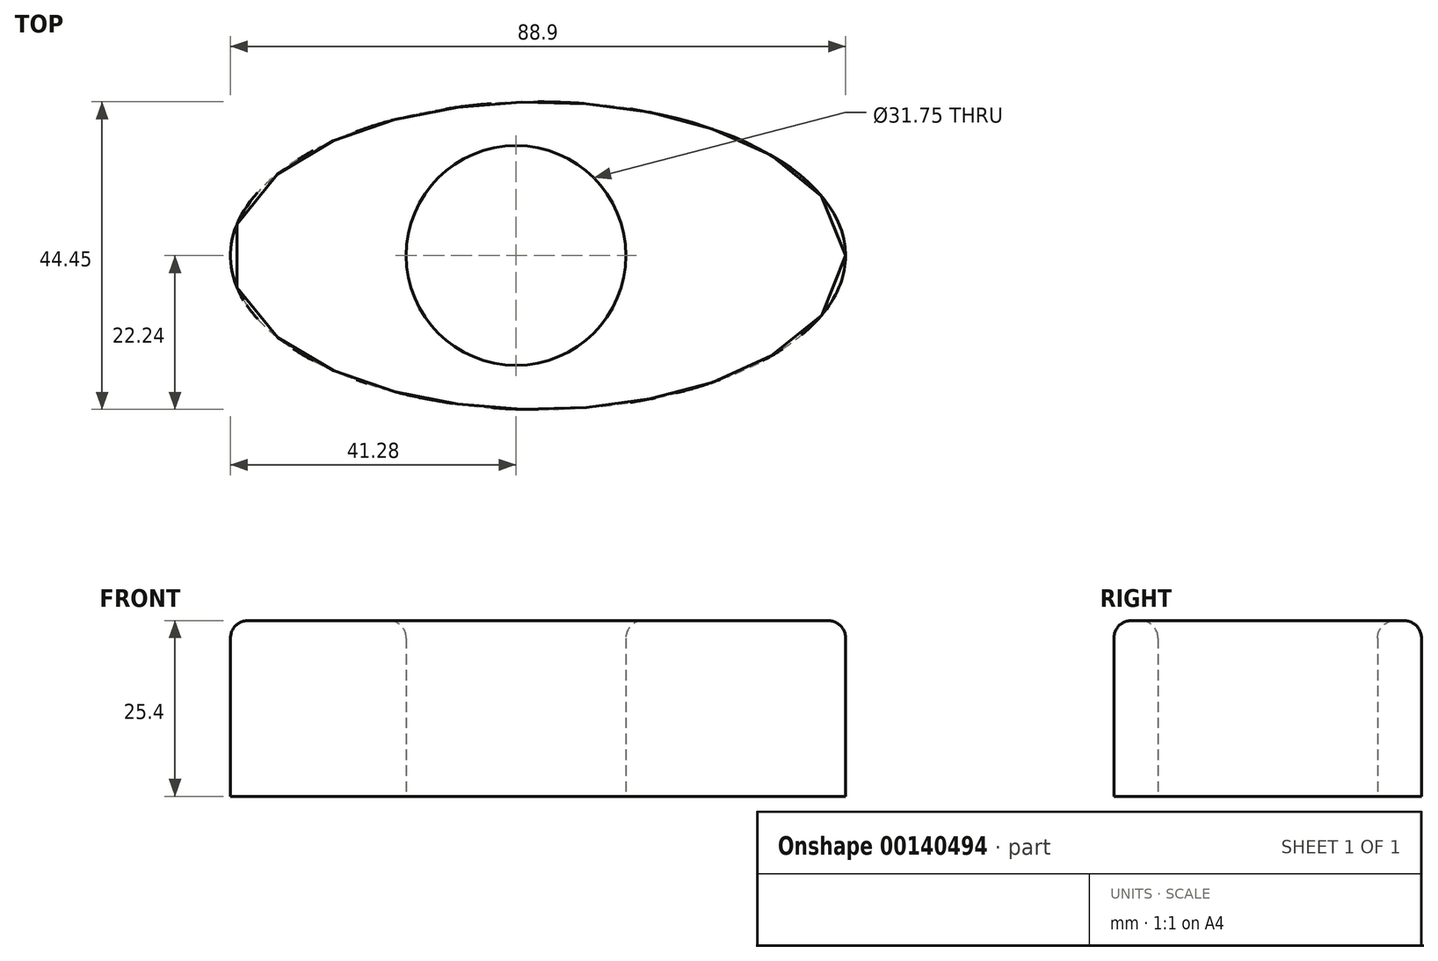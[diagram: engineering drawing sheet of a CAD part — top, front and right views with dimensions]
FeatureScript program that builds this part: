
annotation { "Feature Type Name" : "Feature", "Feature Type Description" : "" }
export const myFeature = defineFeature(function(context is Context, id is Id, definition is map)
    precondition{}
    {
        {
            var Q0;
            Q0=qCreatedBy(makeId("Top.planeOp"),FACE);
            var sketch = newSketch(context, id + "F0", { "sketchPlane" : qUnion([Q0])});
            skCircle(sketch, "E0", {"center": v(0, 0) * mm, "radius": 15.88 * mm});
            skEllipse(sketch, "E1", {"center": v(3.17, -0.02) * mm, "majorRadius": 44.45 * mm, "minorRadius": 22.23 * mm, "majorAxis": v(1, 0)});
            skLineSegment(sketch, "E2.direction1", {"start": v(0, 0) * mm, "end": v(47.62, 0) * mm, "construction": true});
            skLineSegment(sketch, "E3", {"start": v(-15.88, 0) * mm, "end": v(-41.28, 0) * mm});
            skPoint(sketch, "E4.orphan", {"position": v(73.03, 0) * mm});
            skPoint(sketch, "E5.orphan", {"position": v(57.15, 0) * mm});
            skSolve(sketch);
        }
        {
            var Q0;
            Q0=makeQuery(id+"F0.imprint","IMPRINT",FACE,{"disambiguationData":[TD([[makeQuery(id+"F0.imprint","IMPRINT",EDGE,{"derivedFrom":sQuery(id+"F0.wireOp",EDGE,"E0")}),-1.0]])]});
            extrude(context, id + "F1", {"entities" : qUnion([Q0]), "depth" : 25.4 * mm});
        }
        {
            var Q0;
            Q0=makeQuery(id+"F1.opExtrude","CAP_EDGE",EDGE,{"disambiguationData":[OSD([sQuery(id+"F0.wireOp",EDGE,"E1")])],"isStart":false});
            fillet(context, id + "F2", {"entities" : qUnion([Q0]), "radius" : 2.54 * mm, "tangentPropagation" : true, "allowEdgeOverflow" : false});
        }
        {
            var Q0;
            Q0=makeQuery(id+"F1.opExtrude","CAP_EDGE",EDGE,{"disambiguationData":[OSD([sQuery(id+"F0.wireOp",EDGE,"E0")])],"isStart":false});
            var Q1;
            Q1=makeQuery(id+"F1.opExtrude","CAP_EDGE",EDGE,{"disambiguationData":[OSD([sQuery(id+"F0.wireOp",EDGE,"E2.1.0.0")])],"isStart":false});
            fillet(context, id + "F3", {"entities" : qUnion([Q0, Q1]), "radius" : 2.54 * mm, "tangentPropagation" : true, "allowEdgeOverflow" : false});
        }
    });
